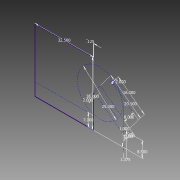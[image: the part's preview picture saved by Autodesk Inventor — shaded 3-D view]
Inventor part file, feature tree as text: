
AUTODESK INVENTOR PART (.ipt)
format: ipt  version: 2014 (Build 180170000, 170)  size: 80,896 bytes
history: native  units: in
note: dims shown in document units (in); Inventor stores cm internally (conversion verified against a paired STEP export)
features: sketch x1
ambient origin geometry x8: Origin, YZ Plane, XZ Plane, XY Plane, X Axis, Y Axis, Z Axis, Center Point
feature tree (1):
  sketch  "Sketch1"  dims[d0=32.5in d1=35.0in d2=7.0in d3=25.0in d5=6.0in d6=0.2542in d7=2.0in d8=20.5in d9=1.0in d10=8.5in d11=1.375in d12=0.125in d13=8.0in d14=18.0in d15=2.0in]
